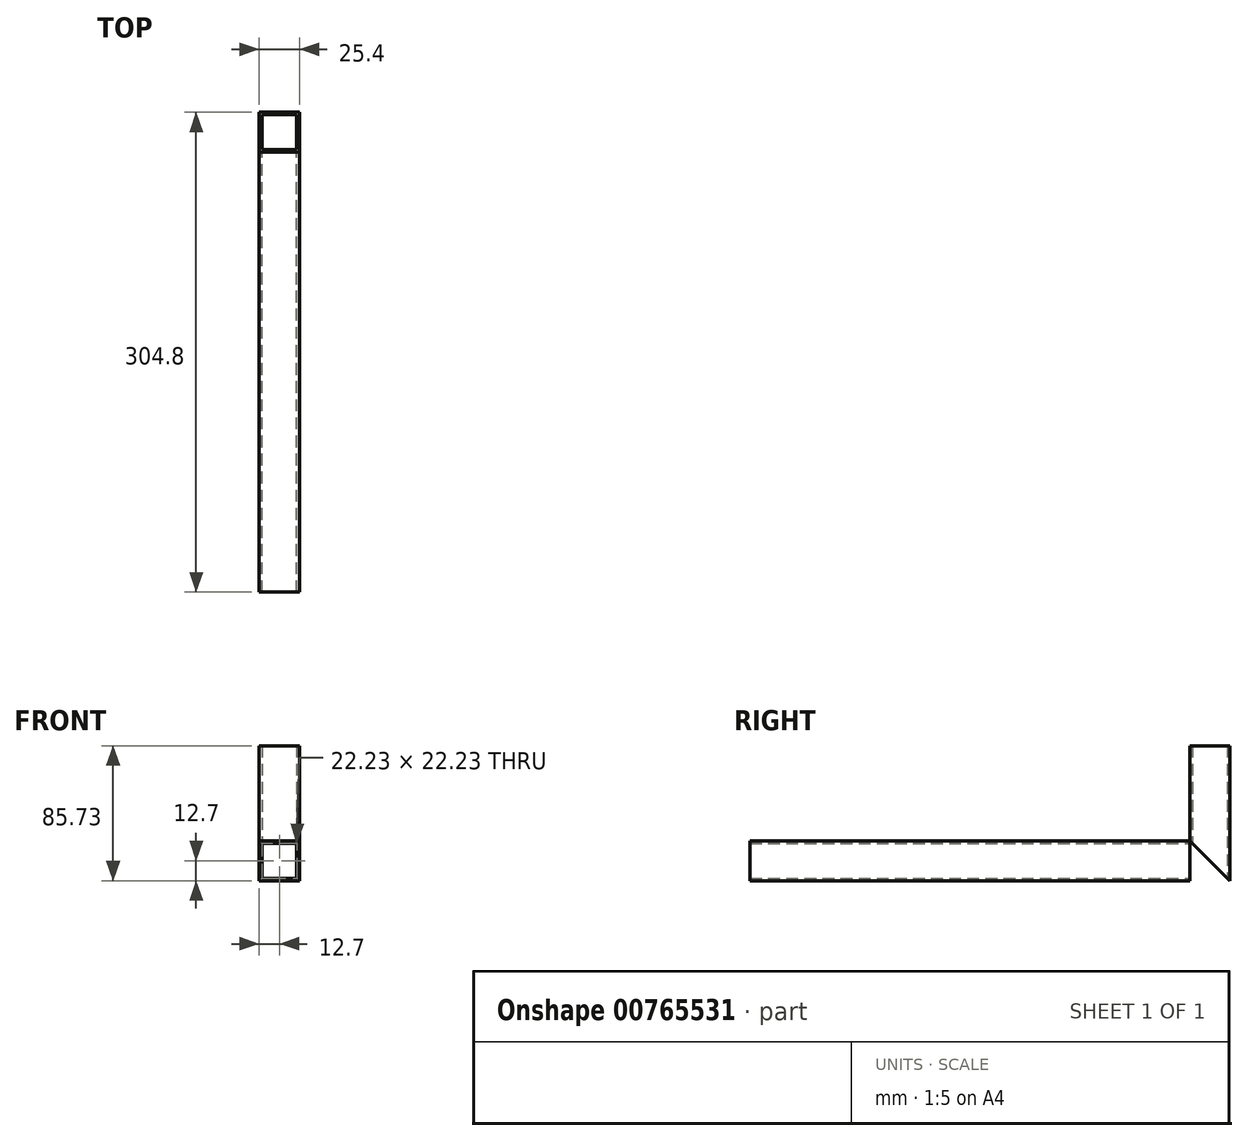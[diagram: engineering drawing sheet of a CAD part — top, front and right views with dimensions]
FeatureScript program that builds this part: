
annotation { "Feature Type Name" : "Feature", "Feature Type Description" : "" }
export const myFeature = defineFeature(function(context is Context, id is Id, definition is map)
    precondition{}
    {
        {
            var Q0;
            Q0=qCreatedBy(makeId("Front.planeOp"),FACE);
            var sketch = newSketch(context, id + "F0", { "sketchPlane" : qUnion([Q0])});
            skLineSegment(sketch, "E0.bottom", {"start": v(-12.7, -12.7) * mm, "end": v(12.7, -12.7) * mm});
            skLineSegment(sketch, "E0.top", {"start": v(-12.7, 12.7) * mm, "end": v(12.7, 12.7) * mm});
            skLineSegment(sketch, "E0.left", {"start": v(12.7, 12.7) * mm, "end": v(12.7, -12.7) * mm});
            skLineSegment(sketch, "E0.right", {"start": v(-12.7, 12.7) * mm, "end": v(-12.7, -12.7) * mm});
            skLineSegment(sketch, "E1", {"start": v(-12.7, 12.7) * mm, "end": v(12.7, -12.7) * mm, "construction": true});
            skLineSegment(sketch, "E2", {"start": v(12.7, 12.7) * mm, "end": v(-12.7, -12.7) * mm, "construction": true});
            skLineSegment(sketch, "E3.0", {"start": v(11.11, 11.11) * mm, "end": v(11.11, -11.11) * mm});
            skLineSegment(sketch, "E3.1", {"start": v(-11.11, 11.11) * mm, "end": v(11.11, 11.11) * mm});
            skLineSegment(sketch, "E3.2", {"start": v(-11.11, 11.11) * mm, "end": v(-11.11, -11.11) * mm});
            skLineSegment(sketch, "E3.3", {"start": v(-11.11, -11.11) * mm, "end": v(11.11, -11.11) * mm});
            skSolve(sketch);
        }
        {
            var Q0;
            Q0 = qSketchRegion(id + "F0", true);
            extrude(context, id + "F1", {"entities" : qUnion([Q0]), "depth" : 304.8 * mm, "offsetDistance" : 25.4 * mm});
        }
        {
            var Q0;
            Q0=qCreatedBy(makeId("Right.planeOp"),FACE);
            var sketch = newSketch(context, id + "F2", { "sketchPlane" : qUnion([Q0])});
            skLineSegment(sketch, "E4.0", {"start": v(0, 12.7) * mm, "end": v(0, -12.7) * mm});
            skLineSegment(sketch, "E5", {"start": v(0, 12.7) * mm, "end": v(-25.4, 12.7) * mm});
            skLineSegment(sketch, "E6", {"start": v(-25.4, 12.7) * mm, "end": v(0, -12.7) * mm});
            skSolve(sketch);
        }
        {
            var Q0;
            Q0 = qSketchRegion(id + "F2", true);
            extrude(context, id + "F3", {"entities" : qUnion([Q0]), "operationType" : NewBodyOperationType.REMOVE, "endBound" : BoundingType.THROUGH_ALL, "oppositeDirection" : true, "depth" : 25.4 * mm, "offsetDistance" : 25.4 * mm, "hasSecondDirection" : true, "secondDirectionBound" : BoundingType.THROUGH_ALL, "secondDirectionOppositeDirection" : false, "secondDirectionDepth" : 25.4 * mm});
        }
        {
            var Q0;
            Q0=makeQuery(id+"F1.opExtrude","SWEPT_FACE",FACE,{"disambiguationData":[OSD([sQuery(id+"F0.wireOp",EDGE,"E0.top")])]});
            cPlane(context, id + "F4", {"entities" : qUnion([Q0]), "cplaneType" : CPlaneType.OFFSET, "offset" : 0 * mm, "width" : 152.4 * mm, "height" : 152.4 * mm});
        }
        {
            var Q0;
            Q0=qCreatedBy(id+"F4.planeOp",FACE);
            var sketch = newSketch(context, id + "F5", { "sketchPlane" : qUnion([Q0])});
            skLineSegment(sketch, "E7.bottom", {"start": v(12.7, -25.4) * mm, "end": v(-12.7, -25.4) * mm});
            skLineSegment(sketch, "E7.top", {"start": v(12.7, 0) * mm, "end": v(-12.7, 0) * mm});
            skLineSegment(sketch, "E7.left", {"start": v(12.7, -25.4) * mm, "end": v(12.7, 0) * mm});
            skLineSegment(sketch, "E7.right", {"start": v(-12.7, -25.4) * mm, "end": v(-12.7, 0) * mm});
            skPoint(sketch, "E7.middle", {"position": v(0, -12.7) * mm});
            skLineSegment(sketch, "E8.0", {"start": v(11.11, -23.81) * mm, "end": v(11.11, -1.59) * mm});
            skLineSegment(sketch, "E8.1", {"start": v(11.11, -23.81) * mm, "end": v(-11.11, -23.81) * mm});
            skLineSegment(sketch, "E8.2", {"start": v(-11.11, -23.81) * mm, "end": v(-11.11, -1.59) * mm});
            skLineSegment(sketch, "E8.3", {"start": v(11.11, -1.59) * mm, "end": v(-11.11, -1.59) * mm});
            skSolve(sketch);
        }
        {
            var Q0;
            Q0 = qSketchRegion(id + "F5", true);
            var Q1;
            Q1=makeQuery(id+"F1.opExtrude","SWEPT_BODY",BODY,{"disambiguationData":[OSD([sQuery(id+"F0.wireOp",EDGE,"E0.bottom"),sQuery(id+"F0.wireOp",EDGE,"E0.top"),sQuery(id+"F0.wireOp",EDGE,"E0.left"),sQuery(id+"F0.wireOp",EDGE,"E0.right"),sQuery(id+"F0.wireOp",EDGE,"E3.0"),sQuery(id+"F0.wireOp",EDGE,"E3.1"),sQuery(id+"F0.wireOp",EDGE,"E3.2"),sQuery(id+"F0.wireOp",EDGE,"E3.3")])]});
            extrude(context, id + "F6", {"entities" : qUnion([Q0]), "depth" : 60.32 * mm, "offsetDistance" : 25.4 * mm, "hasSecondDirection" : true, "secondDirectionOppositeDirection" : true, "secondDirectionDepth" : 50.8 * mm, "secondDirectionBoundEntityBody" : qUnion([Q1])});
        }
        {
            var Q0;
            Q0=makeQuery(id+"F6.opExtrude","SWEPT_FACE",FACE,{"disambiguationData":[OSD([sQuery(id+"F5.wireOp",EDGE,"E7.left")])]});
            var sketch = newSketch(context, id + "F7", { "sketchPlane" : qUnion([Q0])});
            skLineSegment(sketch, "E9.0", {"start": v(-25.4, -38.1) * mm, "end": v(0, -38.1) * mm});
            skLineSegment(sketch, "E10.0", {"start": v(-25.4, 12.7) * mm, "end": v(0, -12.7) * mm});
            skLineSegment(sketch, "E11", {"start": v(-25.4, 12.7) * mm, "end": v(-25.4, -38.1) * mm});
            skLineSegment(sketch, "E12", {"start": v(0, -12.7) * mm, "end": v(0, -38.1) * mm});
            skSolve(sketch);
        }
        {
            var Q0;
            Q0 = qSketchRegion(id + "F7", true);
            extrude(context, id + "F8", {"entities" : qUnion([Q0]), "operationType" : NewBodyOperationType.REMOVE, "endBound" : BoundingType.THROUGH_ALL, "oppositeDirection" : true, "depth" : 25.4 * mm, "offsetDistance" : 25.4 * mm});
        }
    });
